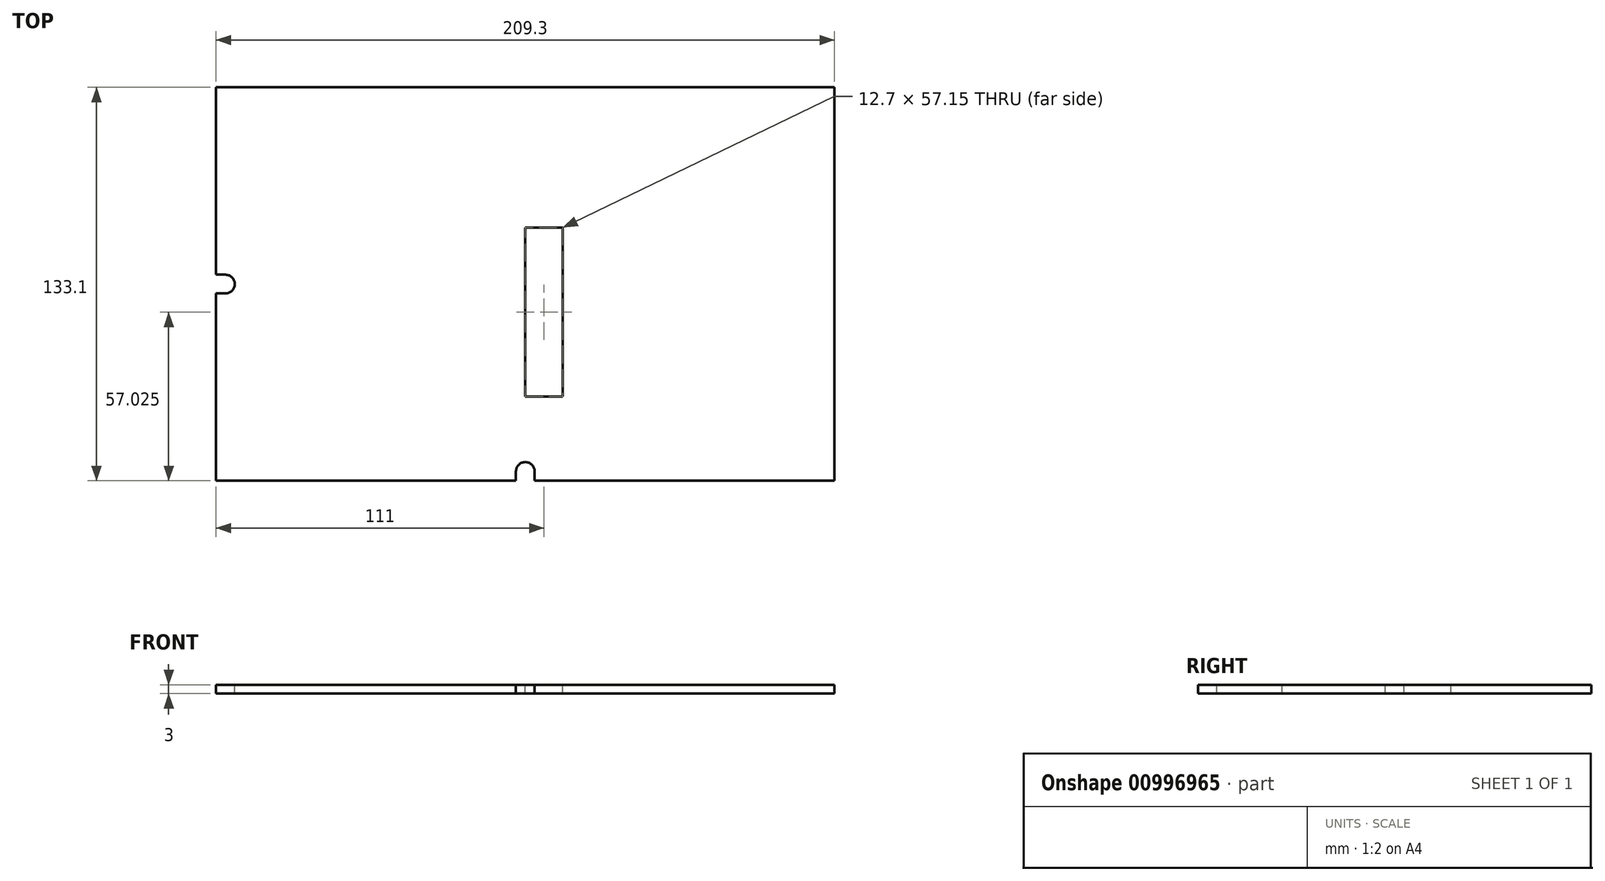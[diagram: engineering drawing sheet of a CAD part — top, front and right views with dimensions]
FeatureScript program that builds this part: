
annotation { "Feature Type Name" : "Feature", "Feature Type Description" : "" }
export const myFeature = defineFeature(function(context is Context, id is Id, definition is map)
    precondition{}
    {
        {
            var Q0;
            Q0=qCreatedBy(makeId("Top.planeOp"),FACE);
            var sketch = newSketch(context, id + "F0", { "sketchPlane" : qUnion([Q0])});
            skLineSegment(sketch, "E0.bottom", {"start": v(104.65, -66.55) * mm, "end": v(-104.65, -66.55) * mm});
            skLineSegment(sketch, "E0.top", {"start": v(104.65, 66.55) * mm, "end": v(-104.65, 66.55) * mm});
            skLineSegment(sketch, "E0.left", {"start": v(104.65, -66.55) * mm, "end": v(104.65, 66.55) * mm});
            skLineSegment(sketch, "E0.right", {"start": v(-104.65, -66.55) * mm, "end": v(-104.65, 66.55) * mm});
            skPoint(sketch, "E0.middle", {"position": v(0, 0) * mm});
            skSolve(sketch);
        }
        {
            var Q0;
            Q0=qSketchRegion(id+"F0",true);
            extrude(context, id + "F1", {"entities" : qUnion([Q0]), "depth" : 3 * mm, "offsetDistance" : 25.4 * mm});
        }
        {
            var Q0;
            Q0=makeQuery(id+"F1.opExtrude","CAP_FACE",FACE,{"disambiguationData":[OSD([sQuery(id+"F0.wireOp",EDGE,"E0.bottom"),sQuery(id+"F0.wireOp",EDGE,"E0.top"),sQuery(id+"F0.wireOp",EDGE,"E0.left"),sQuery(id+"F0.wireOp",EDGE,"E0.right")])],"isStart":false});
            var sketch = newSketch(context, id + "F2", { "sketchPlane" : qUnion([Q0])});
            skLineSegment(sketch, "E1.bottom", {"start": v(0, 19.05) * mm, "end": v(12.7, 19.05) * mm});
            skLineSegment(sketch, "E1.top", {"start": v(0, -38.1) * mm, "end": v(12.7, -38.1) * mm});
            skLineSegment(sketch, "E1.left", {"start": v(0, 19.05) * mm, "end": v(0, -38.1) * mm});
            skLineSegment(sketch, "E1.right", {"start": v(12.7, 19.05) * mm, "end": v(12.7, -38.1) * mm});
            skArc(sketch, "E2", {"start": v(-3.18, -63.37) * mm, "mid": v(0, -60.2) * mm, "end": v(3.18, -63.37) * mm});
            skLineSegment(sketch, "E3", {"start": v(-3.18, -66.55) * mm, "end": v(3.18, -66.55) * mm});
            skLineSegment(sketch, "E4", {"start": v(-3.18, -66.55) * mm, "end": v(-3.18, -63.37) * mm});
            skLineSegment(sketch, "E5", {"start": v(3.17, -63.37) * mm, "end": v(3.17, -66.55) * mm});
            skLineSegment(sketch, "E6", {"start": v(-104.65, 3.17) * mm, "end": v(-104.65, -3.18) * mm});
            skPoint(sketch, "E7", {"position": v(-104.65, 0) * mm});
            skLineSegment(sketch, "E8", {"start": v(-104.65, -3.18) * mm, "end": v(-101.47, -3.18) * mm});
            skLineSegment(sketch, "E9", {"start": v(-104.65, 3.17) * mm, "end": v(-101.47, 3.17) * mm});
            skArc(sketch, "E10", {"start": v(-101.47, -3.17) * mm, "mid": v(-98.3, 0) * mm, "end": v(-101.47, 3.17) * mm});
            skSolve(sketch);
        }
        {
            var Q0;
            Q0=qSketchRegion(id+"F2",true);
            extrude(context, id + "F3", {"entities" : qUnion([Q0]), "operationType" : NewBodyOperationType.REMOVE, "endBound" : BoundingType.THROUGH_ALL, "oppositeDirection" : true, "depth" : 25.4 * mm, "offsetDistance" : 25.4 * mm});
        }
    });
